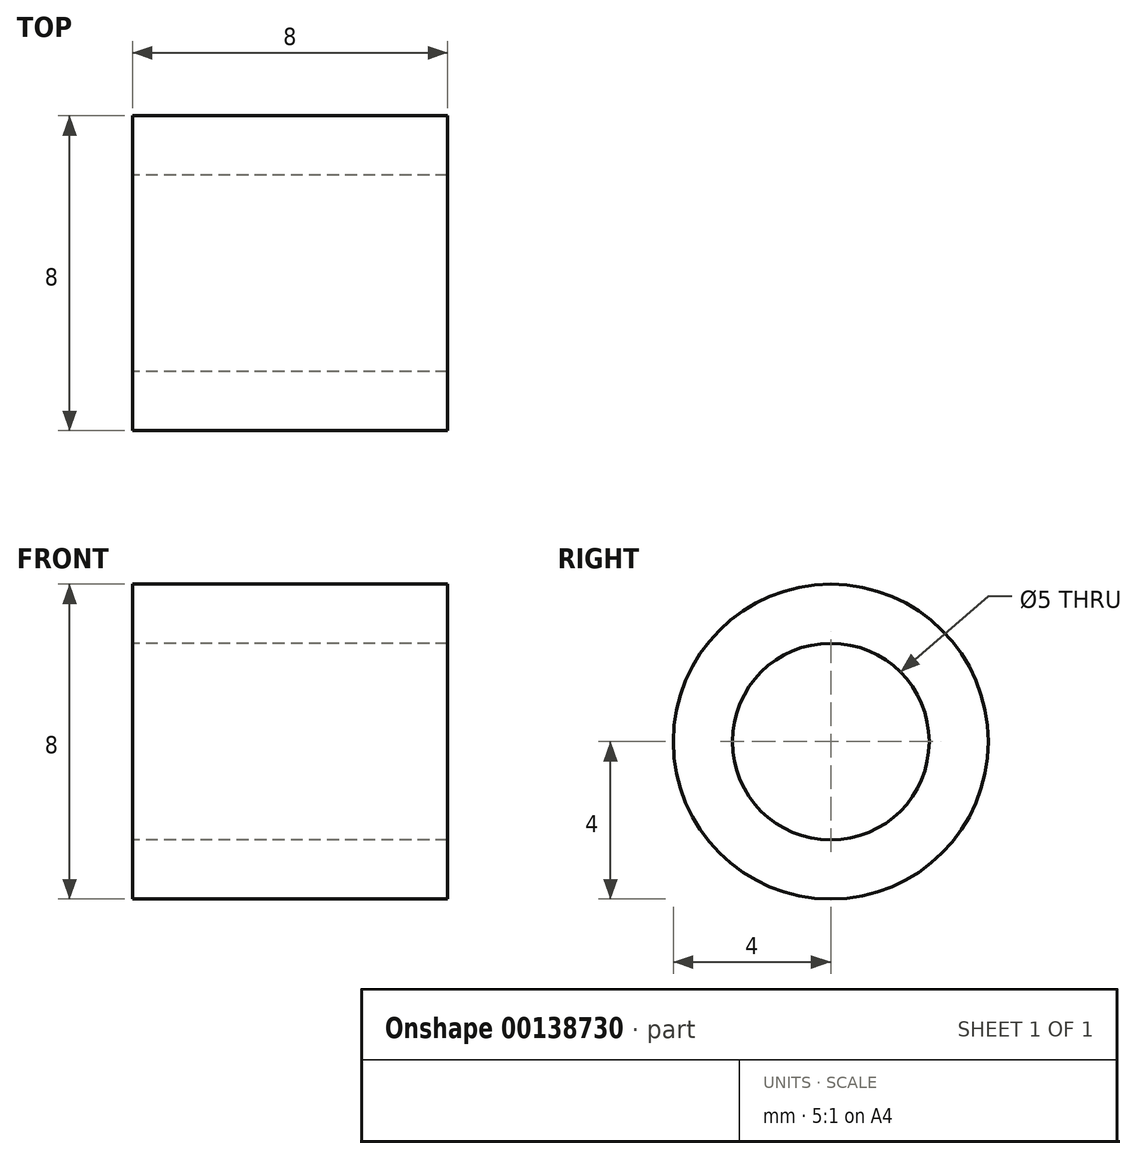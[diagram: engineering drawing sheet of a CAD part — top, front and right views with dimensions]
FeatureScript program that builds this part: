
annotation { "Feature Type Name" : "Feature", "Feature Type Description" : "" }
export const myFeature = defineFeature(function(context is Context, id is Id, definition is map)
    precondition{}
    {
        {
            var Q0;
            Q0=qCreatedBy(makeId("Right.planeOp"),FACE);
            var sketch = newSketch(context, id + "F0", { "sketchPlane" : qUnion([Q0])});
            skCircle(sketch, "E0", {"center": v(0, 0) * mm, "radius": 2.5 * mm});
            skCircle(sketch, "E1", {"center": v(0, 0) * mm, "radius": 4 * mm});
            skSolve(sketch);
        }
        {
            var Q0;
            Q0 = qSketchRegion(id + "F0", true);
            extrude(context, id + "F1", {"entities" : qUnion([Q0]), "depth" : 8 * mm});
        }
    });
